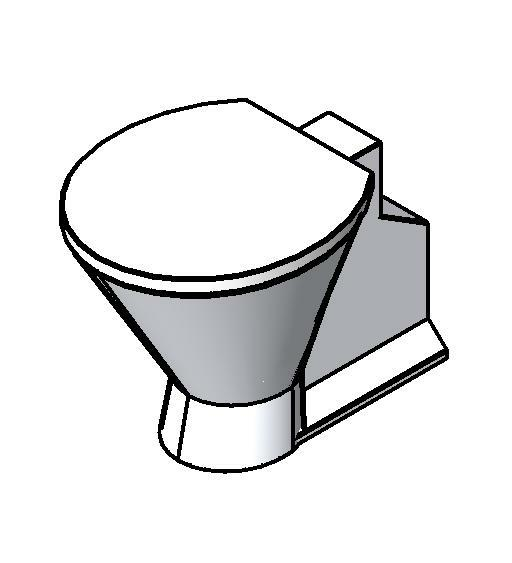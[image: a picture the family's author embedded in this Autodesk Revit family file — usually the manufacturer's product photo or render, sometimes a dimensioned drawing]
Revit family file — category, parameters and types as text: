
# Revit family: 23799-Deca_Misturador Monocomando de Bancada Bica Alta Cromado_Gama_2885-13
name_source: partatom
category: Plumbing Fixtures
units: mm (PartAtom-declared; Revit-internal decimal feet)

## family parameters
Cut with Voids When Loaded = No
Host = Face
Part Type = Normal
Room Calculation Point = No
Round Connector Dimension = Use Radius
Shared = No

## types (1)
- 2885.C13_CROMADO
    Acompanha o Produto = Mangueira Flexivel,Adaptadores de rosca e Deca Comfort
    Aprovado por = quattroD
    Atendimento ao Cliente = 0800 011 7073
    CWFU = 0
    Categoria = METAIS PARA BANHEIRO
    Composição Anel Vedação = -
    Composição Assento = -
    Composição Básica = Liga de Cobre (bronze e latão),Liga de Zinco(zamac),Plásticos de Engenharia,Elastômeros
    Composição Componente = -
    Consumo = -
    Cor Interna = -
    Cor Principal = Cromado
    Cor Secundária = -
    Cores Componente = -
    Criado por = quattroD
    Código Pai = 2885.C13
    Default Elevation = 0 m
    Description = MISTURADOR MONOCOMANDO P/ LAVATORIO MESA BICA ALTA GAMA -CROMADO
    Diâmetro Ponto de Esgoto = 0 m
    Diâmetro Água Fria = 0.02 m
    Informações Complementares = -
    Itens de Instalação = -
    Linha = Gama
    Manufacturer = Deca
    Material = Deca_Cromado
    Model = 2885.C13
    Norma = NBR 15267
    Peso Líquido (Kg) = 1.508
    Raio Ponto de Esgoto = 0 m
    Raio Água Fria = 0.01 m
    Saída de Esgoto = -
    Segmento = -
    Tipo de dispositivo economizador = -
    Tipo de mecanismo utilizado = Cartucho Monocomando
    Tipo de rosca de entrada = BSP NBR 8133
    Tipo de rosca de saída = -
    URL = www.deca.com.br
    WFU = 0

## geometry (parser evidence)
native form markers: Sweep x2
no freeform markers — native parametric forms only
